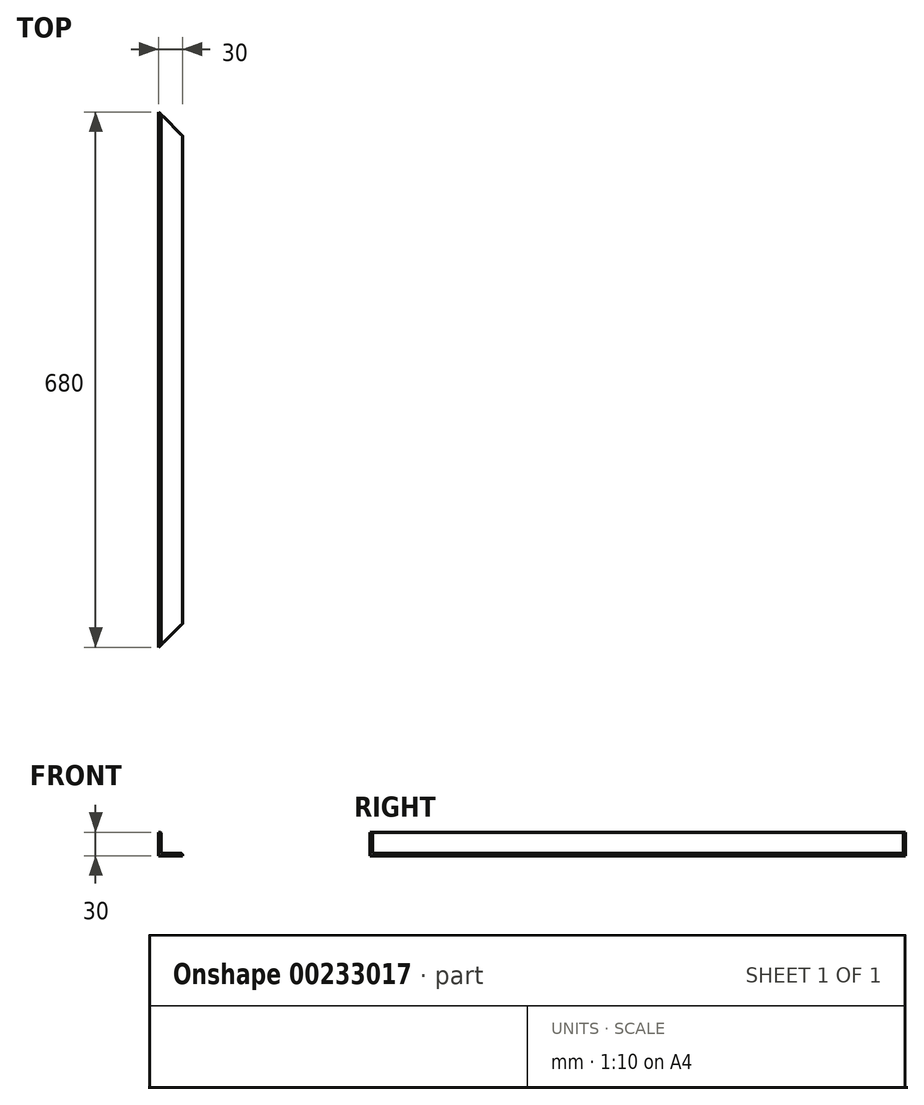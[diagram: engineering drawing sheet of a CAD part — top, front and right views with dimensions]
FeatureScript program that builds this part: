
annotation { "Feature Type Name" : "Feature", "Feature Type Description" : "" }
export const myFeature = defineFeature(function(context is Context, id is Id, definition is map)
    precondition{}
    {
        {
            var Q0;
            Q0=qCreatedBy(makeId("Front.planeOp"),FACE);
            var sketch = newSketch(context, id + "F0", { "sketchPlane" : qUnion([Q0])});
            skLineSegment(sketch, "E0.bottom", {"start": v(0, 0) * mm, "end": v(3, 0) * mm});
            skLineSegment(sketch, "E0.top", {"start": v(0, 30) * mm, "end": v(1.5, 30) * mm});
            skLineSegment(sketch, "E0.left", {"start": v(0, 0) * mm, "end": v(0, 30) * mm});
            skLineSegment(sketch, "E0.right", {"start": v(3, 6) * mm, "end": v(3, 28.5) * mm});
            skLineSegment(sketch, "E1.bottom", {"start": v(0, 0) * mm, "end": v(30, 0) * mm});
            skLineSegment(sketch, "E1.top", {"start": v(6, 3) * mm, "end": v(28.5, 3) * mm});
            skLineSegment(sketch, "E1.left", {"start": v(0, 0) * mm, "end": v(0, 3) * mm});
            skLineSegment(sketch, "E1.right", {"start": v(30, 0) * mm, "end": v(30, 1.5) * mm});
            skPoint(sketch, "E2.visualSharp", {"position": v(3, 3) * mm});
            skArc(sketch, "E2.filletArc", {"start": v(3, 6) * mm, "mid": v(3.88, 3.88) * mm, "end": v(6, 3) * mm});
            skPoint(sketch, "E3.visualSharp", {"position": v(3, 30) * mm});
            skArc(sketch, "E3.filletArc", {"start": v(3, 28.5) * mm, "mid": v(2.56, 29.56) * mm, "end": v(1.5, 30) * mm});
            skPoint(sketch, "E4.visualSharp", {"position": v(30, 3) * mm});
            skArc(sketch, "E4.filletArc", {"start": v(30, 1.5) * mm, "mid": v(29.56, 2.56) * mm, "end": v(28.5, 3) * mm});
            skSolve(sketch);
        }
        {
            var Q0;
            Q0=makeQuery(id+"F0.imprint","IMPRINT",FACE,{"disambiguationData":[TD([[makeQuery(id+"F0.imprint","IMPRINT",EDGE,{"derivedFrom":sQuery(id+"F0.wireOp",EDGE,"E0.top")}),-1.0]])]});
            extrude(context, id + "F1", {"entities" : qUnion([Q0]), "endBound" : BoundingType.SYMMETRIC, "depth" : 680 * mm});
        }
        {
            var Q0;
            Q0=makeQuery(id+"F1.opExtrude","SWEPT_FACE",FACE,{"disambiguationData":[OSD([sQuery(id+"F0.wireOp",EDGE,"E1.bottom")])]});
            var sketch = newSketch(context, id + "F2", { "sketchPlane" : qUnion([Q0])});
            skLineSegment(sketch, "E5", {"start": v(0, 340) * mm, "end": v(30, 310) * mm});
            skLineSegment(sketch, "E6", {"start": v(0, 340) * mm, "end": v(30, 340) * mm});
            skLineSegment(sketch, "E7", {"start": v(30, 340) * mm, "end": v(30, 310) * mm});
            skLineSegment(sketch, "E8.MirrorCS", {"start": v(30, -340) * mm, "end": v(30, -310) * mm});
            skLineSegment(sketch, "E9.MirrorCS", {"start": v(0, -340) * mm, "end": v(30, -340) * mm});
            skLineSegment(sketch, "E10.MirrorCS", {"start": v(0, -340) * mm, "end": v(30, -310) * mm});
            skSolve(sketch);
        }
        {
            var Q0;
            Q0=makeQuery(id+"F2.imprint","IMPRINT",FACE,{"disambiguationData":[TD([[makeQuery(id+"F2.imprint","IMPRINT",EDGE,{"derivedFrom":sQuery(id+"F2.wireOp",EDGE,"E9.MirrorCS")}),1.0]])]});
            var Q1;
            Q1=makeQuery(id+"F2.imprint","IMPRINT",FACE,{"disambiguationData":[TD([[makeQuery(id+"F2.imprint","IMPRINT",EDGE,{"derivedFrom":sQuery(id+"F2.wireOp",EDGE,"E5")}),1.0]])]});
            extrude(context, id + "F3", {"entities" : qUnion([Q0, Q1]), "operationType" : NewBodyOperationType.REMOVE, "endBound" : BoundingType.UP_TO_NEXT, "oppositeDirection" : true, "depth" : 25 * mm});
        }
    });
